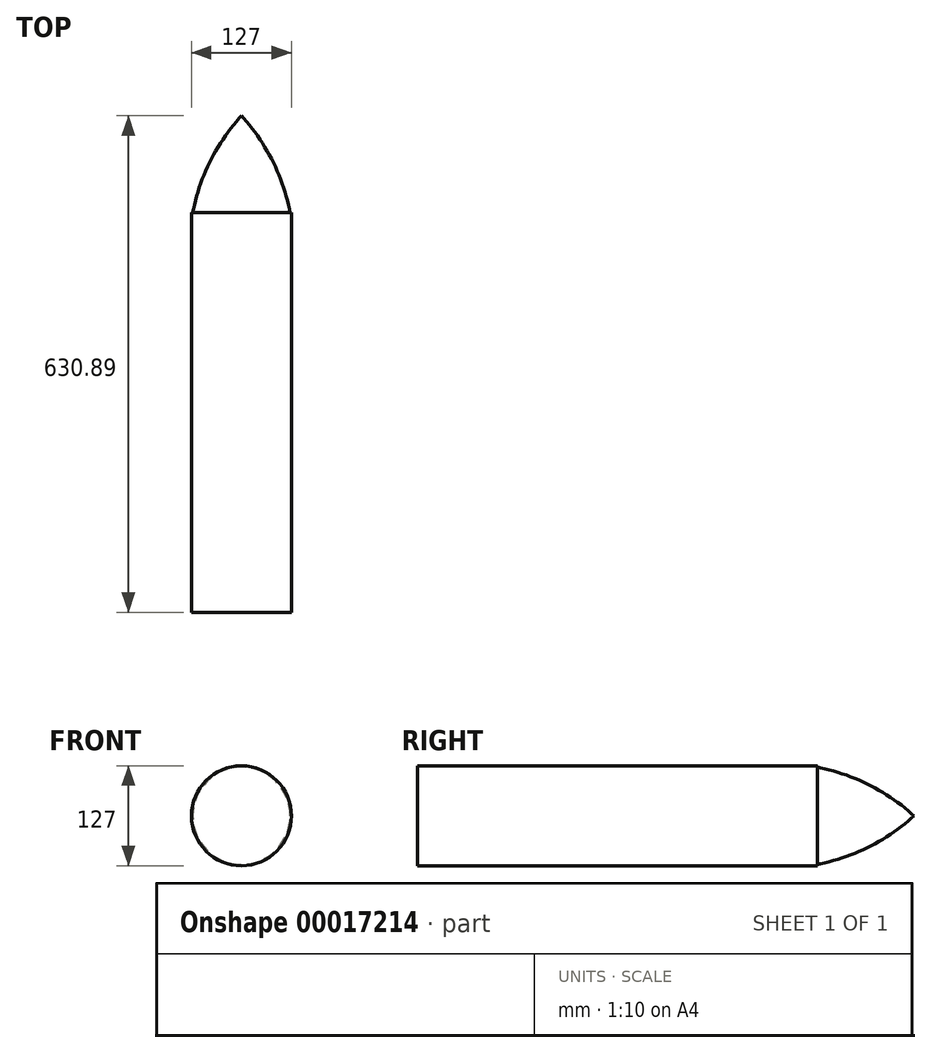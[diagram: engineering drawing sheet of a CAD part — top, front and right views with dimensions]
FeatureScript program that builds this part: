
annotation { "Feature Type Name" : "Feature", "Feature Type Description" : "" }
export const myFeature = defineFeature(function(context is Context, id is Id, definition is map)
    precondition{}
    {
        {
            var Q0;
            Q0=qCreatedBy(makeId("Front.planeOp"),FACE);
            var sketch = newSketch(context, id + "F0", { "sketchPlane" : qUnion([Q0])});
            skCircle(sketch, "E0", {"center": v(0, 0) * mm, "radius": 63.5 * mm});
            skSolve(sketch);
        }
        {
            var Q0;
            Q0 = qSketchRegion(id + "F0", true);
            extrude(context, id + "F1", {"entities" : qUnion([Q0]), "depth" : 508 * mm});
        }
        {
            var Q0;
            Q0=qCreatedBy(makeId("Right.planeOp"),FACE);
            var sketch = newSketch(context, id + "F2", { "sketchPlane" : qUnion([Q0])});
            skLineSegment(sketch, "E1", {"start": v(0, 0) * mm, "end": v(122.89, 0) * mm});
            skLineSegment(sketch, "E2", {"start": v(122.89, 0) * mm, "end": v(119.84, 2.69) * mm});
            skLineSegment(sketch, "E3", {"start": v(3.98, 61) * mm, "end": v(0, 61.84) * mm});
            skLineSegment(sketch, "E4", {"start": v(0, 61.84) * mm, "end": v(0, 0) * mm});
            skPoint(sketch, "E5.visualSharp", {"position": v(69.57, 47.06) * mm});
            skArc(sketch, "E5.filletArc", {"start": v(119.84, 2.69) * mm, "mid": v(65.67, 39.33) * mm, "end": v(3.98, 61) * mm});
            skSolve(sketch);
        }
        {
            var Q0;
            Q0=makeQuery(id+"F2.imprint","IMPRINT",FACE,{"disambiguationData":[TD([[makeQuery(id+"F2.imprint","IMPRINT",EDGE,{"derivedFrom":sQuery(id+"F2.wireOp",EDGE,"E1")}),1.0]])]});
            var Q1;
            Q1=sQuery(id+"F2.wireOp",EDGE,"E1");
            revolve(context, id + "F3", {"operationType" : NewBodyOperationType.ADD, "entities" : qUnion([Q0]), "axis" : qUnion([Q1]), "revolveType" : RevolveType.FULL});
        }
    });
